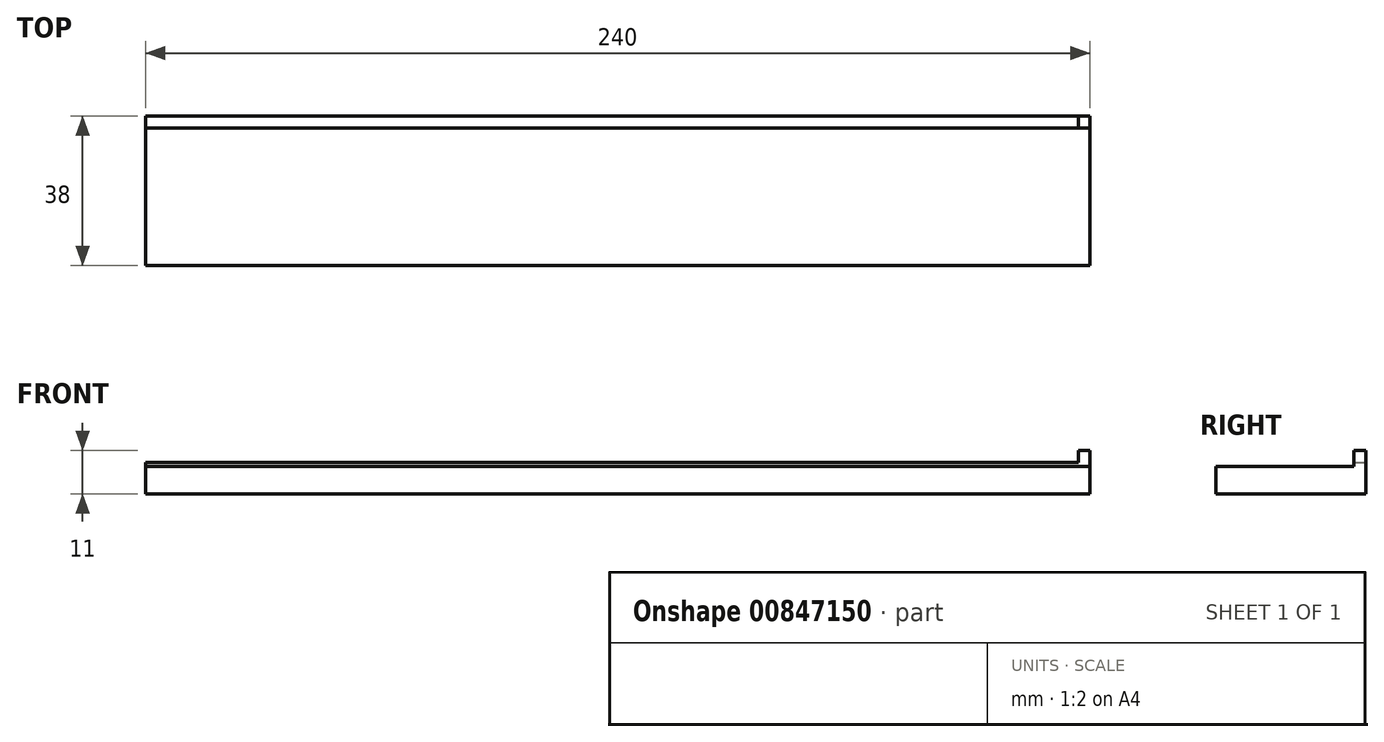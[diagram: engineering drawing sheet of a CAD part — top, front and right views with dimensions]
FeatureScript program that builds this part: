
annotation { "Feature Type Name" : "Feature", "Feature Type Description" : "" }
export const myFeature = defineFeature(function(context is Context, id is Id, definition is map)
    precondition{}
    {
        {
            assignVariable(context, id + "F0", {"name" : "thickness", "anyValue" : 11 - 3});
        }
        {
            var Q0;
            Q0=qCreatedBy(makeId("Top.planeOp"),FACE);
            var sketch = newSketch(context, id + "F1", { "sketchPlane" : qUnion([Q0])});
            skLineSegment(sketch, "E0.bottom", {"start": v(120, -19) * mm, "end": v(-120, -19) * mm});
            skLineSegment(sketch, "E0.top", {"start": v(120, 19) * mm, "end": v(-120, 19) * mm});
            skLineSegment(sketch, "E0.left", {"start": v(120, -19) * mm, "end": v(120, 19) * mm});
            skLineSegment(sketch, "E0.right", {"start": v(-120, -19) * mm, "end": v(-120, 19) * mm});
            skPoint(sketch, "E0.middle", {"position": v(0, 0) * mm});
            skSolve(sketch);
        }
        {
            var Q0;
            Q0 = qSketchRegion(id + "F1", true);
            extrude(context, id + "F2", {"entities" : qUnion([Q0]), "depth" : (getVariable(context, 'thickness')) * mm, "offsetDistance" : 25 * mm});
        }
        {
            var Q0;
            Q0=makeQuery(id+"F2.opExtrude","CAP_FACE",FACE,{"disambiguationData":[OSD([sQuery(id+"F1.wireOp",EDGE,"E0.bottom"),sQuery(id+"F1.wireOp",EDGE,"E0.top"),sQuery(id+"F1.wireOp",EDGE,"E0.left"),sQuery(id+"F1.wireOp",EDGE,"E0.right")])],"isStart":false});
            var sketch = newSketch(context, id + "F3", { "sketchPlane" : qUnion([Q0])});
            skLineSegment(sketch, "E1.bottom", {"start": v(-120, -19) * mm, "end": v(120, -19) * mm});
            skLineSegment(sketch, "E1.top", {"start": v(-120, 16) * mm, "end": v(120, 16) * mm});
            skLineSegment(sketch, "E1.left", {"start": v(-120, -19) * mm, "end": v(-120, 16) * mm});
            skLineSegment(sketch, "E1.right", {"start": v(120, -19) * mm, "end": v(120, 16) * mm});
            skSolve(sketch);
        }
        {
            var Q0;
            Q0 = qSketchRegion(id + "F3", true);
            extrude(context, id + "F4", {"entities" : qUnion([Q0]), "operationType" : NewBodyOperationType.REMOVE, "oppositeDirection" : true, "depth" : 1 * mm, "offsetDistance" : 25 * mm});
        }
        {
            var Q0;
            Q0=makeQuery(id+"F2.opExtrude","CAP_FACE",FACE,{"disambiguationData":[OSD([sQuery(id+"F1.wireOp",EDGE,"E0.bottom"),sQuery(id+"F1.wireOp",EDGE,"E0.top"),sQuery(id+"F1.wireOp",EDGE,"E0.left"),sQuery(id+"F1.wireOp",EDGE,"E0.right")])],"isStart":false});
            var sketch = newSketch(context, id + "F5", { "sketchPlane" : qUnion([Q0])});
            skLineSegment(sketch, "E2.bottom", {"start": v(120, 16) * mm, "end": v(117, 16) * mm});
            skLineSegment(sketch, "E2.top", {"start": v(120, 19) * mm, "end": v(117, 19) * mm});
            skLineSegment(sketch, "E2.left", {"start": v(120, 16) * mm, "end": v(120, 19) * mm});
            skLineSegment(sketch, "E2.right", {"start": v(117, 16) * mm, "end": v(117, 19) * mm});
            skSolve(sketch);
        }
        {
            var Q0;
            Q0 = qSketchRegion(id + "F5", true);
            extrude(context, id + "F6", {"entities" : qUnion([Q0]), "operationType" : NewBodyOperationType.ADD, "depth" : 3 * mm, "offsetDistance" : 25 * mm});
        }
    });
